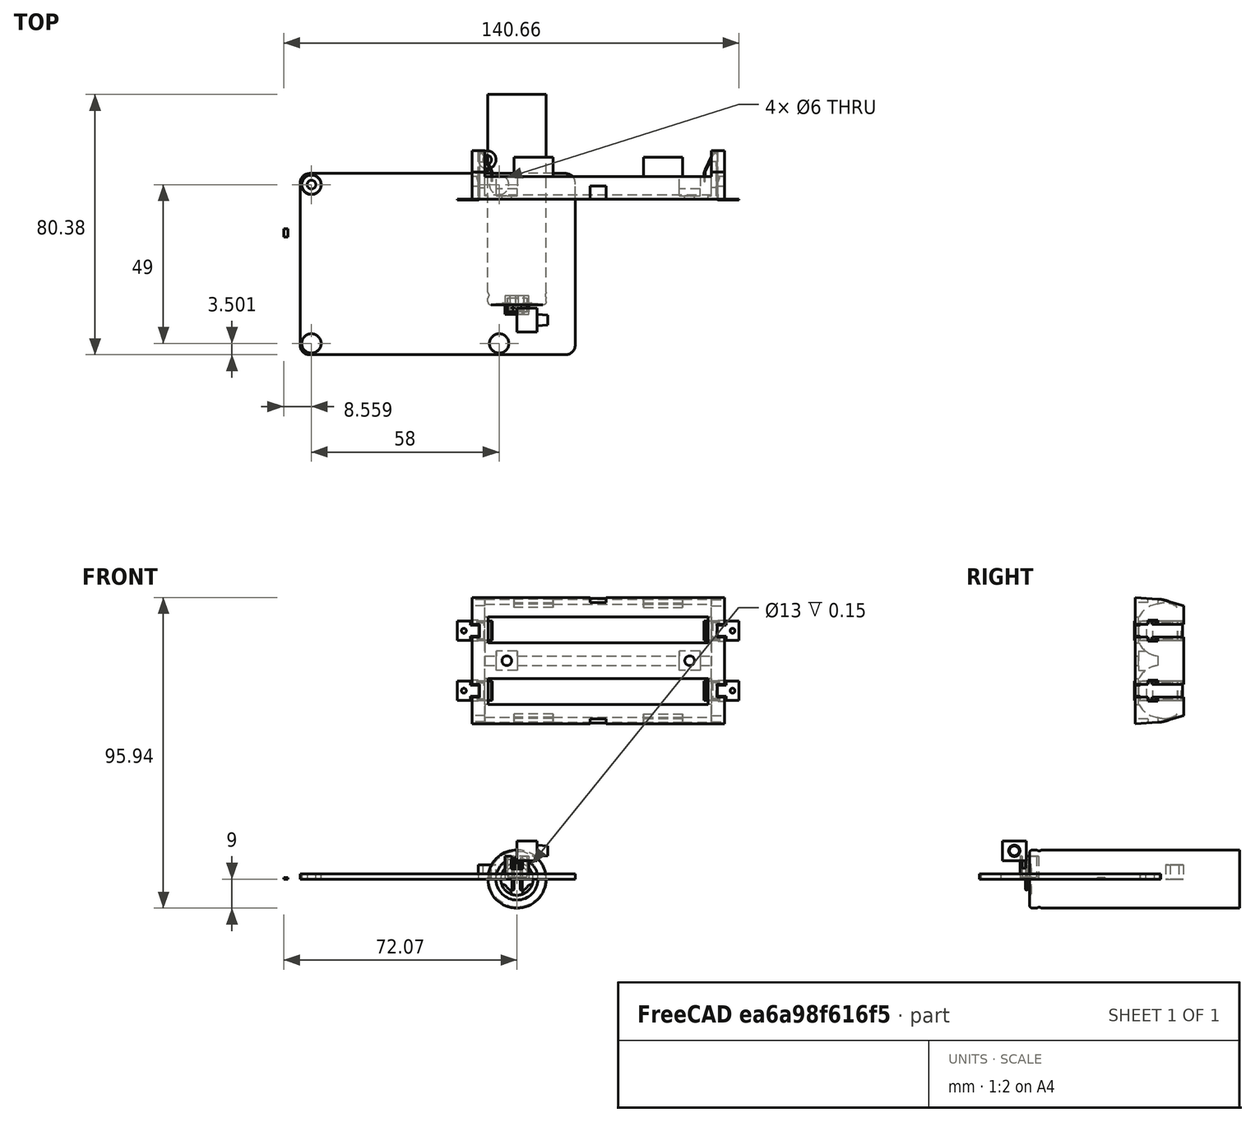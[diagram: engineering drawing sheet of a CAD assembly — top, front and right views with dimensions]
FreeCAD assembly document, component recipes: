
FREECAD ASSEMBLY — COMPONENT RECIPES ("UPS")

This assembly document has 22 components, labeled P0..P21 below (a component is one placed body or linked part). 17 of them carry a construction recipe — the FreeCAD feature program that regenerates the part from scratch, quoted from this document or its linked companion documents; the rest are supplied as boundary geometry only. No exploded tour is included for this assembly.
COMPONENT P0 — recipe-attached ("Board001", modeled in this document).
Construction recipe (the document's own serialized feature program — sketch geometry with constraints, then the solid features built on it; lengths are millimeters unless a unit is written):

FEATURE [Sketcher::SketchObject] Sketch
  ArcFitTolerance = 1e-06
  FullyConstrained = false
  MakeInternals = false
  sketch-geometry (20):
    g0: LineSegment StartX=-64.0111 StartY=-15.3795 StartZ=0 EndX=14.9889 EndY=-15.3795 EndZ=0
    g1: LineSegment StartX=17.9889 StartY=-12.3795 StartZ=0 EndX=17.9889 EndY=37.6205 EndZ=0
    g2: LineSegment StartX=14.9889 StartY=40.6205 StartZ=0 EndX=-64.0111 EndY=40.6205 EndZ=0
    g3: LineSegment StartX=-67.0111 StartY=37.6205 StartZ=0 EndX=-67.0111 EndY=-12.3795 EndZ=0
    g4: ArcOfCircle CenterX=14.9889 CenterY=37.6205 CenterZ=0 NormalX=0 NormalY=0 NormalZ=1 AngleXU=0 Radius=3 StartAngle=5e-16 EndAngle=1.5708
    g5: GeomPoint [constr] X=17.9889 Y=40.6205 Z=0
    g6: ArcOfCircle CenterX=-64.0111 CenterY=37.6205 CenterZ=0 NormalX=0 NormalY=0 NormalZ=1 AngleXU=0 Radius=3 StartAngle=1.5708 EndAngle=3.14159
    g7: GeomPoint [constr] X=-67.0111 Y=40.6205 Z=0
    g8: ArcOfCircle CenterX=-64.0111 CenterY=-12.3795 CenterZ=0 NormalX=0 NormalY=0 NormalZ=1 AngleXU=0 Radius=3 StartAngle=3.14159 EndAngle=4.71239
    g9: GeomPoint [constr] X=-67.0111 Y=-15.3795 Z=0
    g10: ArcOfCircle CenterX=14.9889 CenterY=-12.3795 CenterZ=0 NormalX=0 NormalY=0 NormalZ=1 AngleXU=0 Radius=3 StartAngle=4.71239 EndAngle=6.28319
    g11: GeomPoint [constr] X=17.9889 Y=-15.3795 Z=0
    g12: Circle CenterX=-63.5111 CenterY=37.1205 CenterZ=0 NormalX=0 NormalY=0 NormalZ=1 AngleXU=0 Radius=1.35
    g13: Circle CenterX=-63.5111 CenterY=37.1205 CenterZ=0 NormalX=0 NormalY=0 NormalZ=1 AngleXU=0 Radius=3
    g14: Circle CenterX=-63.5111 CenterY=-11.8795 CenterZ=0 NormalX=0 NormalY=0 NormalZ=1 AngleXU=0 Radius=1.35
    g15: Circle CenterX=-63.5111 CenterY=-11.8795 CenterZ=0 NormalX=0 NormalY=0 NormalZ=1 AngleXU=0 Radius=3
    g16: Circle CenterX=-5.51111 CenterY=37.1205 CenterZ=0 NormalX=0 NormalY=0 NormalZ=1 AngleXU=0 Radius=1.35
    g17: Circle CenterX=-5.51111 CenterY=37.1205 CenterZ=0 NormalX=0 NormalY=0 NormalZ=1 AngleXU=0 Radius=3
    g18: Circle CenterX=-5.51111 CenterY=-11.8795 CenterZ=0 NormalX=0 NormalY=0 NormalZ=1 AngleXU=0 Radius=1.35
    g19: Circle CenterX=-5.51111 CenterY=-11.8795 CenterZ=0 NormalX=0 NormalY=0 NormalZ=1 AngleXU=0 Radius=3
  constraints (46):
    c: Horizontal(g0)
    c: Horizontal(g2)
    c: Vertical(g1)
    c: Vertical(g3)
    c: DistanceX(g7,g5) = 85
    c: DistanceY(g9,g7) = 56
    c: PointOnObject(g5,g1)
    c: PointOnObject(g5,g2)
    c: Tangent(g1,g4) = -1.5708
    c: Tangent(g2,g4) = -1.5708
    c: PointOnObject(g7,g2)
    c: PointOnObject(g7,g3)
    c: Tangent(g2,g6) = -1.5708
    c: Tangent(g3,g6) = -1.5708
    c: PointOnObject(g9,g0)
    c: PointOnObject(g9,g3)
    c: Tangent(g0,g8) = -1.5708
    c: Tangent(g3,g8) = -1.5708
    c: PointOnObject(g11,g0)
    c: PointOnObject(g11,g1)
    c: Tangent(g0,g10) = -1.5708
    c: Tangent(g1,g10) = -1.5708
    c: Radius(g6) = 3
    c: Radius(g8) = 3
    c: Radius(g4) = 3
    c: Radius(g10) = 3
    c: Diameter(g12) = 2.7
    c: Coincident(g13,g12)
    c: Diameter(g13) = 6
    c: Diameter(g14) = 2.7
    c: Coincident(g15,g14)
    c: Diameter(g15) = 6
    c: Vertical(g14,g12)
    c: Distance(g13,g15) = 43
    c: Distance(g13,g3) = 0.5
    c: Distance(g13,g2) = 0.5
    c: Diameter(g16) = 2.7
    c: Coincident(g17,g16)
    c: Diameter(g17) = 6
    c: Diameter(g18) = 2.7
    c: Coincident(g19,g18)
    c: Diameter(g19) = 6
    c: Vertical(g18,g16)
    c: Distance(g17,g19) = 43
    c: Distance(g15,g19) = 52
    c: Horizontal(g18,g14)
FEATURE [PartDesign::Pad] Pad
  Direction = (0,0,1)
  Length = 1.6
  Length2 = 10
  Profile = -> Sketch
  ReferenceAxis = -> Sketch [N_Axis]
  Refine = true
  Suppressed = false
  Type = 0
FEATURE [PartDesign::Body] Body  label="Board"
  AllowCompound = false
  Group = -> [Sketch,Pad]
  Origin = -> Origin
  Tip = -> Pad
COMPONENT P1 — recipe-attached ("Button001", modeled in this document).
Construction recipe (the document's own serialized feature program — sketch geometry with constraints, then the solid features built on it; lengths are millimeters unless a unit is written):

FEATURE [Sketcher::SketchObject] Sketch003
  ArcFitTolerance = 1e-06
  AttachmentSupport = -> [YZ_Plane009]
  FullyConstrained = false
  MakeInternals = false
  MapMode = 5
  Placement = pos=(0,0,0) rot=(0.57735,0.57735,0.57735;2.0944rad)
  sketch-geometry (4):
    g0: LineSegment StartX=-8.34718 StartY=11.7111 StartZ=0 EndX=-8.34718 EndY=5.71105 EndZ=0
    g1: LineSegment StartX=-8.34718 StartY=5.71105 StartZ=0 EndX=-0.947178 EndY=5.71105 EndZ=0
    g2: LineSegment StartX=-0.947178 StartY=5.71105 StartZ=0 EndX=-0.947178 EndY=11.7111 EndZ=0
    g3: LineSegment StartX=-0.947178 StartY=11.7111 StartZ=0 EndX=-8.34718 EndY=11.7111 EndZ=0
  constraints (10):
    c: Coincident(g0,g1)
    c: Coincident(g1,g2)
    c: Coincident(g2,g3)
    c: Coincident(g3,g0)
    c: Vertical(g0)
    c: Vertical(g2)
    c: Horizontal(g1)
    c: Horizontal(g3)
    c: DistanceX(g3,g3) = 7.4
    c: DistanceY(g0,g0) = 6
FEATURE [PartDesign::Pad] Pad003
  Direction = (1,0,0)
  Length = 6.25
  Length2 = 10
  Placement = pos=(0,0,0) rot=(1,1,1;2.0944rad)
  Profile = -> Sketch003
  ReferenceAxis = -> Sketch003 [N_Axis]
  Refine = true
  Suppressed = false
  Type = 0
FEATURE [Sketcher::SketchObject] Sketch004
  ArcFitTolerance = 1e-06
  AttachmentSupport = -> [Pad003]
  ExternalGeometry = -> [Pad003]
  FullyConstrained = true
  MakeInternals = false
  MapMode = 5
  Placement = pos=(6.25,-1.4e-15,7e-16) rot=(0.57735,0.57735,0.57735;2.0944rad)
  sketch-geometry (3):
    g0: GeomPoint X=-4.64718 Y=11.7111 Z=0
    g1: GeomPoint X=-8.34718 Y=8.71105 Z=0
    g2: Circle CenterX=-4.64718 CenterY=8.71105 CenterZ=0 NormalX=0 NormalY=0 NormalZ=1 AngleXU=0 Radius=1.5
  constraints (5):
    c: Symmetric(g-3,g-3,g0)
    c: Symmetric(g-4,g-4,g1)
    c: Diameter(g2) = 3
    c: Vertical(g2,g0)
    c: Horizontal(g1,g2)
FEATURE [PartDesign::Pad] Pad004
  BaseFeature = -> Pad003
  Direction = (1,0,0)
  Length = 3.25
  Length2 = 10
  Placement = pos=(0,0,0) rot=(1,1,1;2.0944rad)
  Profile = -> Sketch004
  ReferenceAxis = -> Sketch004 [N_Axis]
  Refine = true
  Suppressed = false
  Type = 0
FEATURE [PartDesign::Chamfer] Chamfer
  Angle = 85.55
  Base = -> Pad004 [Edge13]
  BaseFeature = -> Pad004
  ChamferType = 2
  FlipDirection = false
  Placement = pos=(0,0,0) rot=(1,1,1;2.0944rad)
  Refine = true
  Size = 0.25
  Size2 = 1
  SupportTransform = false
  Suppressed = false
  UseAllEdges = false
FEATURE [PartDesign::Body] Body003  label="Button"
  AllowCompound = false
  Group = -> [Sketch003,Pad003,Sketch004,Pad004,Chamfer]
  Origin = -> Origin009
  Tip = -> Chamfer
COMPONENT P2 — recipe-attached ("LED001", modeled in this document).
Construction recipe (the document's own serialized feature program — sketch geometry with constraints, then the solid features built on it; lengths are millimeters unless a unit is written):

FEATURE [Sketcher::SketchObject] Sketch005
  ArcFitTolerance = 1e-06
  AttachmentSupport = -> [XY_Plane010]
  FullyConstrained = false
  MakeInternals = false
  MapMode = 5
  sketch-geometry (4):
    g0: LineSegment StartX=-72.0667 StartY=23.4887 StartZ=0 EndX=-72.0667 EndY=20.9887 EndZ=0
    g1: LineSegment StartX=-72.0667 StartY=20.9887 StartZ=0 EndX=-70.8167 EndY=20.9887 EndZ=0
    g2: LineSegment StartX=-70.8167 StartY=20.9887 StartZ=0 EndX=-70.8167 EndY=23.4887 EndZ=0
    g3: LineSegment StartX=-70.8167 StartY=23.4887 StartZ=0 EndX=-72.0667 EndY=23.4887 EndZ=0
  constraints (10):
    c: Coincident(g0,g1)
    c: Coincident(g1,g2)
    c: Coincident(g2,g3)
    c: Coincident(g3,g0)
    c: Vertical(g0)
    c: Vertical(g2)
    c: Horizontal(g1)
    c: Horizontal(g3)
    c: DistanceY(g2,g2) = 2.5
    c: Distance(g3,g3) = 1.25
FEATURE [PartDesign::Pad] Pad005
  Direction = (0,0,1)
  Length = 0.5
  Length2 = 10
  Profile = -> Sketch005
  ReferenceAxis = -> Sketch005 [N_Axis]
  Refine = true
  Suppressed = false
  Type = 0
FEATURE [PartDesign::Body] Body004  label="LED"
  AllowCompound = false
  Group = -> [Sketch005,Pad005]
  Origin = -> Origin010
  Tip = -> Pad005
COMPONENT P3 — same part as P2; its construction recipe is shown at P2.
COMPONENT P4 — same part as P2; its construction recipe is shown at P2.
COMPONENT P5 — same part as P2; its construction recipe is shown at P2.
COMPONENT P6 — same part as P2; its construction recipe is shown at P2.
COMPONENT P7 — same part as P2; its construction recipe is shown at P2.
COMPONENT P8 — same part as P2; its construction recipe is shown at P2.
COMPONENT P9 — recipe-attached ("Screw Insert001", modeled in this document).
Construction recipe (the document's own serialized feature program — sketch geometry with constraints, then the solid features built on it; lengths are millimeters unless a unit is written):

FEATURE [Sketcher::SketchObject] Sketch001
  ArcFitTolerance = 1e-06
  AttachmentSupport = -> [XY_Plane003]
  FullyConstrained = false
  MakeInternals = false
  MapMode = 5
  sketch-geometry (2):
    g0: Circle CenterX=-63.4811 CenterY=37.1626 CenterZ=0 NormalX=0 NormalY=0 NormalZ=1 AngleXU=0 Radius=3
    g1: Circle CenterX=-63.4811 CenterY=37.1626 CenterZ=0 NormalX=0 NormalY=0 NormalZ=1 AngleXU=0 Radius=1.35
  constraints (3):
    c: Diameter(g0) = 6
    c: Coincident(g1,g0)
    c: Diameter(g1) = 2.7
FEATURE [PartDesign::Pad] Pad001
  Direction = (0,0,1)
  Length = 1.6
  Length2 = 10
  Profile = -> Sketch001
  ReferenceAxis = -> Sketch001 [N_Axis]
  Refine = true
  Suppressed = false
  Type = 0
FEATURE [PartDesign::Body] Body001  label="Screw Insert"
  AllowCompound = false
  Group = -> [Sketch001,Pad001]
  Origin = -> Origin003
  Tip = -> Pad001
COMPONENT P10 — same part as P9; its construction recipe is shown at P9.
COMPONENT P11 — same part as P9; its construction recipe is shown at P9.
COMPONENT P12 — same part as P9; its construction recipe is shown at P9.
COMPONENT P13 — recipe-attached ("Spacer001", modeled in this document).
Construction recipe (the document's own serialized feature program — sketch geometry with constraints, then the solid features built on it; lengths are millimeters unless a unit is written):

FEATURE [Sketcher::SketchObject] Sketch002
  ArcFitTolerance = 1e-06
  AttachmentSupport = -> [XY_Plane008]
  FullyConstrained = false
  MakeInternals = false
  MapMode = 5
  sketch-geometry (2):
    g0: Circle CenterX=-9.21613 CenterY=44.8635 CenterZ=0 NormalX=0 NormalY=0 NormalZ=1 AngleXU=0 Radius=2.75
    g1: Circle CenterX=-9.21613 CenterY=44.8635 CenterZ=0 NormalX=0 NormalY=0 NormalZ=1 AngleXU=0 Radius=1.35
  constraints (3):
    c: Diameter(g0) = 5.5
    c: Coincident(g1,g0)
    c: Diameter(g1) = 2.7
FEATURE [PartDesign::Pad] Pad002
  Direction = (0,0,1)
  Length = 4.4
  Length2 = 10
  Profile = -> Sketch002
  ReferenceAxis = -> Sketch002 [N_Axis]
  Refine = true
  Suppressed = false
  Type = 0
FEATURE [PartDesign::Body] Body002  label="Spacer"
  AllowCompound = false
  Group = -> [Sketch002,Pad002]
  Origin = -> Origin008
  Tip = -> Pad002
COMPONENT P14 — same part as P13; its construction recipe is shown at P13.
COMPONENT P15 — same part as P13; its construction recipe is shown at P13.
COMPONENT P16 — same part as P13; its construction recipe is shown at P13.
COMPONENT P17 — geometry summary ("XH 2,54_2p008"; no construction recipe available for this part):
  bounding box: 10.4 x 7.4 x 5.8 mm
  tessellated surface: 356 triangles
  volume: 118 mm^3 (27% of its bounding box)
  symmetry: mirror-symmetric across its x mid-plane
COMPONENT P18 — geometry summary ("XH 2,54_2p009"; no construction recipe available for this part):
  bounding box: 10.4 x 7.4 x 5.8 mm
  tessellated surface: 356 triangles
  volume: 118 mm^3 (27% of its bounding box)
  symmetry: mirror-symmetric across its x mid-plane
COMPONENT P19 — geometry summary ("18650 Battery Holder001"; no construction recipe available for this part):
  bounding box: 87.0 x 39.0 x 15.3 mm
  tessellated surface: 15,868 triangles
  volume: 9904 mm^3 (19% of its bounding box)
  symmetry: 2-fold rotationally symmetric about the z axis; mirror-symmetric across its y mid-plane
COMPONENT P20 — geometry summary ("18650 v003"; no construction recipe available for this part):
  bounding box: 65.0 x 18.0 x 18.0 mm
  tessellated surface: 25,056 triangles
  volume: 16488 mm^3 (78% of its bounding box)
  symmetry: revolution-symmetric about the x axis through its bounding-box center; 2-fold rotationally symmetric about the z axis; mirror-symmetric across its x mid-plane, y mid-plane, z mid-plane
COMPONENT P21 — geometry summary ("18650 v002"; no construction recipe available for this part):
  bounding box: 65.0 x 18.0 x 18.0 mm
  tessellated surface: 25,056 triangles
  volume: 16488 mm^3 (78% of its bounding box)
  symmetry: revolution-symmetric about the x axis through its bounding-box center; 2-fold rotationally symmetric about the z axis; mirror-symmetric across its x mid-plane, y mid-plane, z mid-plane
PROVENANCE & LICENSES
A FreeCAD (.FCStd) document from a public repository crawl; recipes are the document's own serialized feature recipes (and, for linked parts, companion documents' recipes).
License: as declared in the source repository (recorded in the dataset sidecar).
